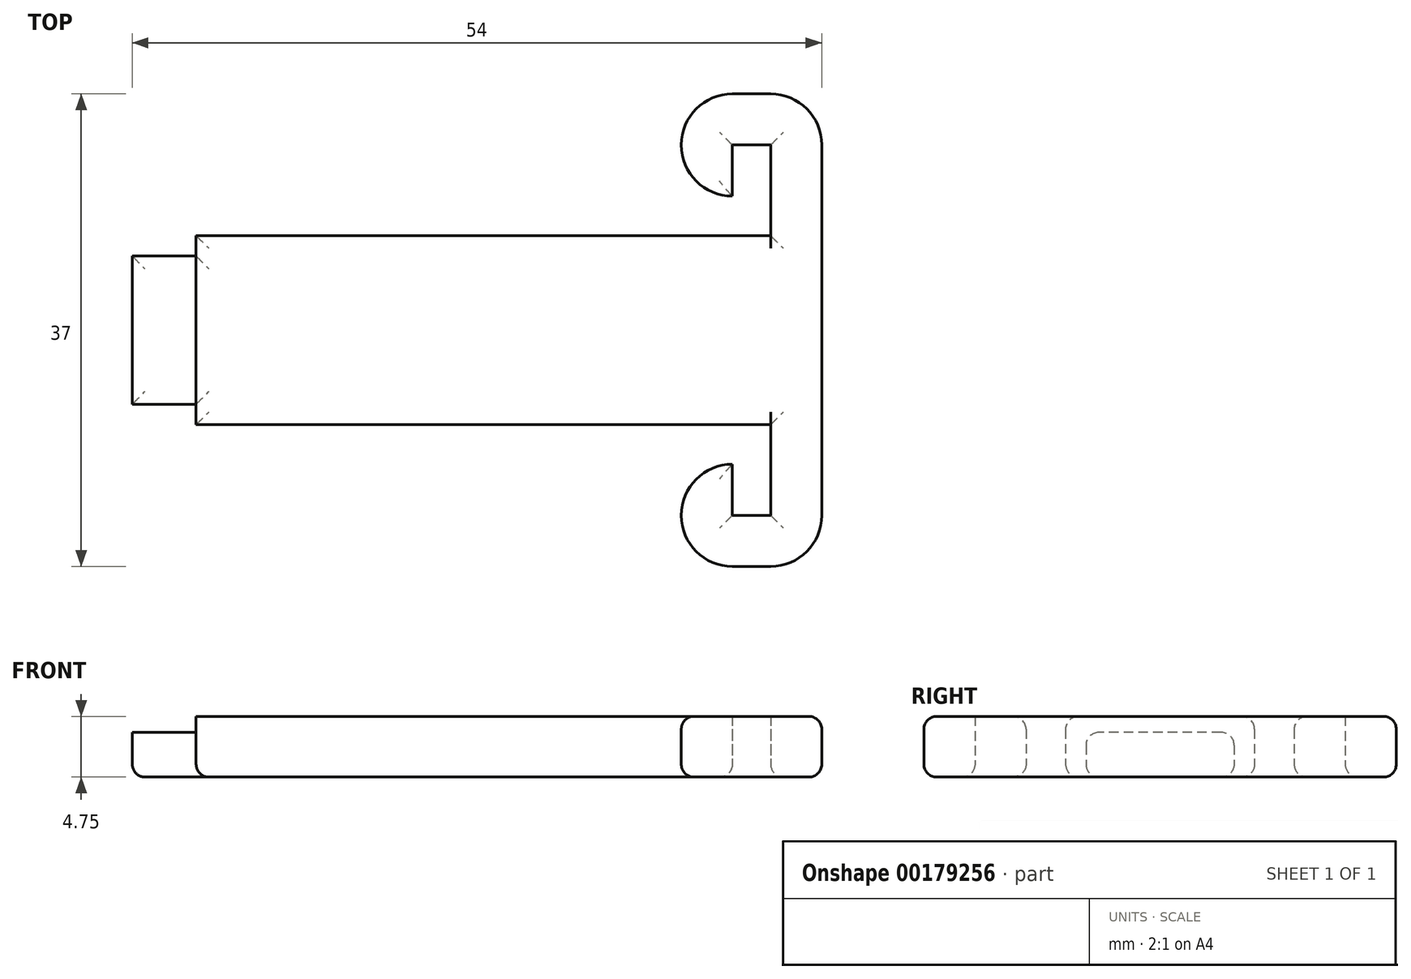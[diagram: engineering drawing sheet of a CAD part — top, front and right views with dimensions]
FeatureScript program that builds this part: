
annotation { "Feature Type Name" : "Feature", "Feature Type Description" : "" }
export const myFeature = defineFeature(function(context is Context, id is Id, definition is map)
    precondition{}
    {
        {
            var Q0;
            Q0=qCreatedBy(makeId("Top.planeOp"),FACE);
            var sketch = newSketch(context, id + "F0", { "sketchPlane" : qUnion([Q0])});
            skLineSegment(sketch, "E0.bottom", {"start": v(-50, 5.8) * mm, "end": v(-45, 5.8) * mm});
            skLineSegment(sketch, "E0.top", {"start": v(-50, -5.8) * mm, "end": v(-45, -5.8) * mm});
            skLineSegment(sketch, "E0.left", {"start": v(-50, 5.8) * mm, "end": v(-50, -5.8) * mm});
            skLineSegment(sketch, "E0.right", {"start": v(-45, 5.8) * mm, "end": v(-45, -5.8) * mm});
            skLineSegment(sketch, "E1", {"start": v(-45, 5.8) * mm, "end": v(-45, 7.4) * mm});
            skLineSegment(sketch, "E2", {"start": v(-45, 7.4) * mm, "end": v(0, 7.4) * mm});
            skLineSegment(sketch, "E3", {"start": v(0, 7.4) * mm, "end": v(0, 14.5) * mm});
            skLineSegment(sketch, "E4", {"start": v(0, 14.5) * mm, "end": v(-3, 14.5) * mm});
            skLineSegment(sketch, "E5", {"start": v(-3, 14.5) * mm, "end": v(-3, 10.5) * mm});
            skLineSegment(sketch, "E6", {"start": v(-3, 10.5) * mm, "end": v(-3, 10.5) * mm});
            skLineSegment(sketch, "E7", {"start": v(-7, 14.5) * mm, "end": v(-7, 14.5) * mm});
            skLineSegment(sketch, "E8", {"start": v(-3, 18.5) * mm, "end": v(0, 18.5) * mm});
            skLineSegment(sketch, "E9", {"start": v(4, 14.5) * mm, "end": v(4, 0) * mm});
            skPoint(sketch, "E10.visualSharp", {"position": v(-7, 18.5) * mm});
            skArc(sketch, "E10.filletArc", {"start": v(-3, 18.5) * mm, "mid": v(-5.83, 17.33) * mm, "end": v(-7, 14.5) * mm});
            skPoint(sketch, "E11.visualSharp", {"position": v(4, 18.5) * mm});
            skArc(sketch, "E11.filletArc", {"start": v(4, 14.5) * mm, "mid": v(2.83, 17.33) * mm, "end": v(0, 18.5) * mm});
            skPoint(sketch, "E12.visualSharp", {"position": v(-7, 10.5) * mm});
            skArc(sketch, "E12.filletArc", {"start": v(-7, 14.5) * mm, "mid": v(-5.83, 11.67) * mm, "end": v(-3, 10.5) * mm});
            skLineSegment(sketch, "E13.MirrorCS", {"start": v(-45, -5.8) * mm, "end": v(-45, -7.4) * mm});
            skArc(sketch, "E14.MirrorCS", {"start": v(-7, -14.5) * mm, "mid": v(-5.83, -11.67) * mm, "end": v(-3, -10.5) * mm});
            skPoint(sketch, "E15.MirrorP", {"position": v(4, -18.5) * mm});
            skArc(sketch, "E16.MirrorCS", {"start": v(4, -14.5) * mm, "mid": v(2.83, -17.33) * mm, "end": v(0, -18.5) * mm});
            skPoint(sketch, "E17.MirrorP", {"position": v(-7, -18.5) * mm});
            skLineSegment(sketch, "E18.MirrorCS", {"start": v(-50, -5.8) * mm, "end": v(-50, 5.8) * mm});
            skArc(sketch, "E19.MirrorCS", {"start": v(-3, -18.5) * mm, "mid": v(-5.83, -17.33) * mm, "end": v(-7, -14.5) * mm});
            skLineSegment(sketch, "E20.MirrorCS", {"start": v(-7, -14.5) * mm, "end": v(-7, -14.5) * mm});
            skLineSegment(sketch, "E21.MirrorCS", {"start": v(-3, -18.5) * mm, "end": v(0, -18.5) * mm});
            skLineSegment(sketch, "E22.MirrorCS", {"start": v(4, -14.5) * mm, "end": v(4, 0) * mm});
            skLineSegment(sketch, "E23.MirrorCS", {"start": v(-45, -5.8) * mm, "end": v(-45, 5.8) * mm});
            skLineSegment(sketch, "E24.MirrorCS", {"start": v(-3, -10.5) * mm, "end": v(-3, -10.5) * mm});
            skLineSegment(sketch, "E25.MirrorCS", {"start": v(-3, -14.5) * mm, "end": v(-3, -10.5) * mm});
            skLineSegment(sketch, "E26.MirrorCS", {"start": v(0, -14.5) * mm, "end": v(-3, -14.5) * mm});
            skLineSegment(sketch, "E27.MirrorCS", {"start": v(-45, -7.4) * mm, "end": v(0, -7.4) * mm});
            skPoint(sketch, "E28.MirrorP", {"position": v(-7, -10.5) * mm});
            skLineSegment(sketch, "E29.MirrorCS", {"start": v(0, -7.4) * mm, "end": v(0, -14.5) * mm});
            skSolve(sketch);
        }
        {
            var Q0;
            Q0=makeQuery(id+"F0.imprint","IMPRINT",FACE,{"disambiguationData":[TD([[makeQuery(id+"F0.imprint","IMPRINT",EDGE,{"derivedFrom":sQuery(id+"F0.wireOp",EDGE,"E1")}),-1.0]])]});
            extrude(context, id + "F1", {"entities" : qUnion([Q0]), "depth" : 4.75 * mm});
        }
        {
            var Q0;
            Q0=makeQuery(id+"F0.imprint","IMPRINT",FACE,{"disambiguationData":[TD([[makeQuery(id+"F0.imprint","IMPRINT",EDGE,{"derivedFrom":sQuery(id+"F0.wireOp",EDGE,"E0.top")}),1.0]])]});
            extrude(context, id + "F2", {"entities" : qUnion([Q0]), "operationType" : NewBodyOperationType.ADD, "depth" : 3.5 * mm});
        }
        {
            var Q0;
            Q0=makeQuery(id+"F2.opExtrude","CAP_EDGE",EDGE,{"disambiguationData":[OSD([sQuery(id+"F0.wireOp",EDGE,"E0.top")])],"isStart":false});
            var Q1;
            Q1=makeQuery(id+"F2.opExtrude","CAP_EDGE",EDGE,{"disambiguationData":[OSD([sQuery(id+"F0.wireOp",EDGE,"E0.bottom")])],"isStart":false});
            var Q2;
            Q2=makeQuery(id+"F1.opExtrude","CAP_EDGE",EDGE,{"disambiguationData":[OSD([sQuery(id+"F0.wireOp",EDGE,"E27.MirrorCS")])],"isStart":false});
            var Q3;
            Q3=makeQuery(id+"F1.opExtrude","CAP_EDGE",EDGE,{"disambiguationData":[OSD([sQuery(id+"F0.wireOp",EDGE,"E2")])],"isStart":false});
            var Q4;
            Q4=makeQuery(id+"F1.opExtrude","CAP_EDGE",EDGE,{"disambiguationData":[OSD([sQuery(id+"F0.wireOp",EDGE,"E10.filletArc"),sQuery(id+"F0.wireOp",EDGE,"E12.filletArc")])],"isStart":false});
            var Q5;
            {var subQ0=sQuery(id+"F0.wireOp",EDGE,"E23.MirrorCS");Q5=makeQuery(id+"F2.boolean.opBoolean","MERGE",FACE,{"derivedFrom":[makeQuery(id+"F1.opExtrude","CAP_FACE",FACE,{"disambiguationData":[OSD([sQuery(id+"F0.wireOp",EDGE,"E1"),sQuery(id+"F0.wireOp",EDGE,"E2"),sQuery(id+"F0.wireOp",EDGE,"E3"),sQuery(id+"F0.wireOp",EDGE,"E4"),sQuery(id+"F0.wireOp",EDGE,"E5"),sQuery(id+"F0.wireOp",EDGE,"E8"),sQuery(id+"F0.wireOp",EDGE,"E9"),sQuery(id+"F0.wireOp",EDGE,"E10.filletArc"),sQuery(id+"F0.wireOp",EDGE,"E11.filletArc"),sQuery(id+"F0.wireOp",EDGE,"E12.filletArc"),sQuery(id+"F0.wireOp",EDGE,"E13.MirrorCS"),sQuery(id+"F0.wireOp",EDGE,"E14.MirrorCS"),sQuery(id+"F0.wireOp",EDGE,"E16.MirrorCS"),sQuery(id+"F0.wireOp",EDGE,"E19.MirrorCS"),sQuery(id+"F0.wireOp",EDGE,"E21.MirrorCS"),sQuery(id+"F0.wireOp",EDGE,"E22.MirrorCS"),subQ0,sQuery(id+"F0.wireOp",EDGE,"E25.MirrorCS"),sQuery(id+"F0.wireOp",EDGE,"E26.MirrorCS"),sQuery(id+"F0.wireOp",EDGE,"E27.MirrorCS"),sQuery(id+"F0.wireOp",EDGE,"E29.MirrorCS")])],"isStart":true}),makeQuery(id+"F2.opExtrude","CAP_FACE",FACE,{"disambiguationData":[OSD([sQuery(id+"F0.wireOp",EDGE,"E0.top"),sQuery(id+"F0.wireOp",EDGE,"E0.bottom"),sQuery(id+"F0.wireOp",EDGE,"E18.MirrorCS"),subQ0])],"isStart":true})]});}
            fillet(context, id + "F3", {"entities" : qUnion([Q0, Q1, Q2, Q3, Q4, Q5]), "radius" : 1 * mm, "tangentPropagation" : true, "defaultsChanged" : false, "vertexSettings" : [], "allowEdgeOverflow" : false});
        }
    });
